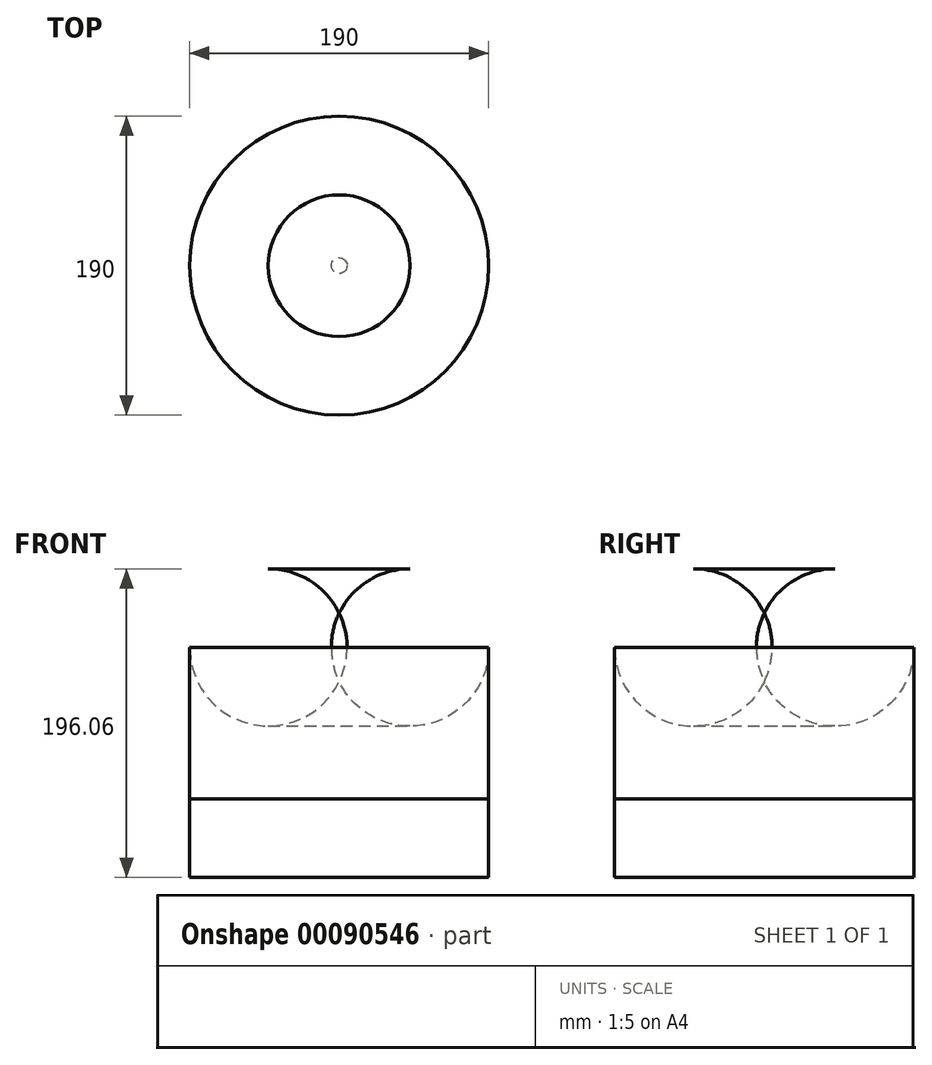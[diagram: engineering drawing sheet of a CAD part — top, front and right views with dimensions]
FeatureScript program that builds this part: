
annotation { "Feature Type Name" : "Feature", "Feature Type Description" : "" }
export const myFeature = defineFeature(function(context is Context, id is Id, definition is map)
    precondition{}
    {
        {
            var Q0;
            Q0=qCreatedBy(makeId("Right.planeOp"),FACE);
            var sketch = newSketch(context, id + "F0", { "sketchPlane" : qUnion([Q0])});
            skLineSegment(sketch, "E0", {"start": v(0, 0) * mm, "end": v(0, 146.06) * mm});
            skLineSegment(sketch, "E1", {"start": v(0, 146.06) * mm, "end": v(95, 146.06) * mm});
            skLineSegment(sketch, "E2", {"start": v(95, 146.06) * mm, "end": v(95, 0) * mm});
            skLineSegment(sketch, "E3", {"start": v(95, 0) * mm, "end": v(0, 0) * mm});
            skSolve(sketch);
        }
        {
            var Q0;
            Q0=makeQuery(id+"F0.imprint","IMPRINT",FACE,{"disambiguationData":[TD([[makeQuery(id+"F0.imprint","IMPRINT",EDGE,{"derivedFrom":sQuery(id+"F0.wireOp",EDGE,"E0")}),-1.0]])]});
            var Q1;
            Q1=sQuery(id+"F0.wireOp",EDGE,"E0");
            revolve(context, id + "F1", {"entities" : qUnion([Q0]), "axis" : qUnion([Q1]), "revolveType" : RevolveType.FULL});
        }
        {
            var Q0;
            Q0=makeQuery(id+"F1.opRevolve","SWEPT_EDGE",EDGE,{"disambiguationData":[OSD([sQuery(id+"F0.wireOp",EDGE,"E1"),sQuery(id+"F0.wireOp",EDGE,"E2")])]});
            fillet(context, id + "F2", {"entities" : qUnion([Q0]), "radius" : 50 * mm, "tangentPropagation" : true, "allowEdgeOverflow" : false});
        }
        {
            var Q0;
            Q0=makeQuery(id+"F1.opRevolve","SWEPT_FACE",FACE,{"disambiguationData":[OSD([sQuery(id+"F0.wireOp",EDGE,"E3")])]});
            var sketch = newSketch(context, id + "F3", { "sketchPlane" : qUnion([Q0])});
            skCircle(sketch, "E4", {"center": v(0, 0) * mm, "radius": 95 * mm});
            skSolve(sketch);
        }
        {
            var Q0;
            Q0=makeQuery(id+"F3.imprint","IMPRINT",FACE,{"disambiguationData":[TD([[makeQuery(id+"F3.imprint","IMPRINT",EDGE,{"derivedFrom":sQuery(id+"F3.wireOp",EDGE,"E4")}),1.0]])]});
            extrude(context, id + "F4", {"entities" : qUnion([Q0]), "depth" : 50 * mm});
        }
    });
